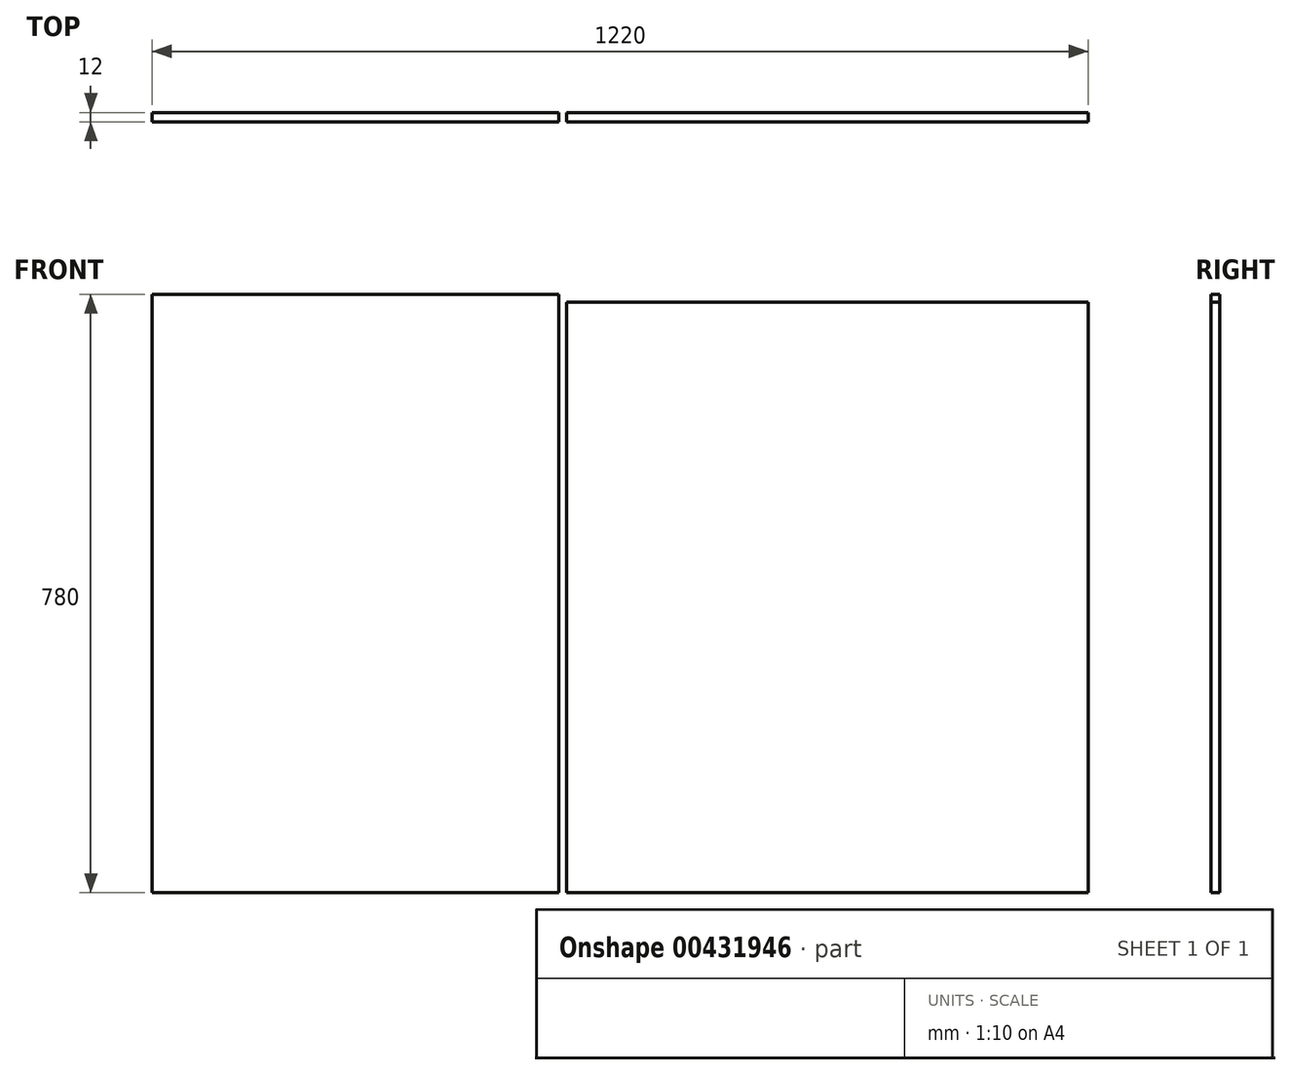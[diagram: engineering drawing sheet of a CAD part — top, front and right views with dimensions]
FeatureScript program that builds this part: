
annotation { "Feature Type Name" : "Feature", "Feature Type Description" : "" }
export const myFeature = defineFeature(function(context is Context, id is Id, definition is map)
    precondition{}
    {
        {
            var Q0;
            Q0=qCreatedBy(makeId("Front.planeOp"),FACE);
            var sketch = newSketch(context, id + "F0", { "sketchPlane" : qUnion([Q0])});
            skLineSegment(sketch, "E0.bottom", {"start": v(0, 0) * mm, "end": v(-530, 0) * mm});
            skLineSegment(sketch, "E0.top", {"start": v(0, 780) * mm, "end": v(-530, 780) * mm});
            skLineSegment(sketch, "E0.left", {"start": v(0, 0) * mm, "end": v(0, 780) * mm});
            skLineSegment(sketch, "E0.right", {"start": v(-530, 0) * mm, "end": v(-530, 780) * mm});
            skLineSegment(sketch, "E1.bottom", {"start": v(10, 0) * mm, "end": v(690, 0) * mm});
            skLineSegment(sketch, "E1.top", {"start": v(10, 770) * mm, "end": v(690, 770) * mm});
            skLineSegment(sketch, "E1.left", {"start": v(10, 0) * mm, "end": v(10, 770) * mm});
            skLineSegment(sketch, "E1.right", {"start": v(690, 0) * mm, "end": v(690, 770) * mm});
            skSolve(sketch);
        }
        {
            var Q0;
            Q0 = qSketchRegion(id + "F0", true);
            extrude(context, id + "F1", {"entities" : qUnion([Q0]), "depth" : 12 * mm, "offsetDistance" : 25 * mm});
        }
    });
